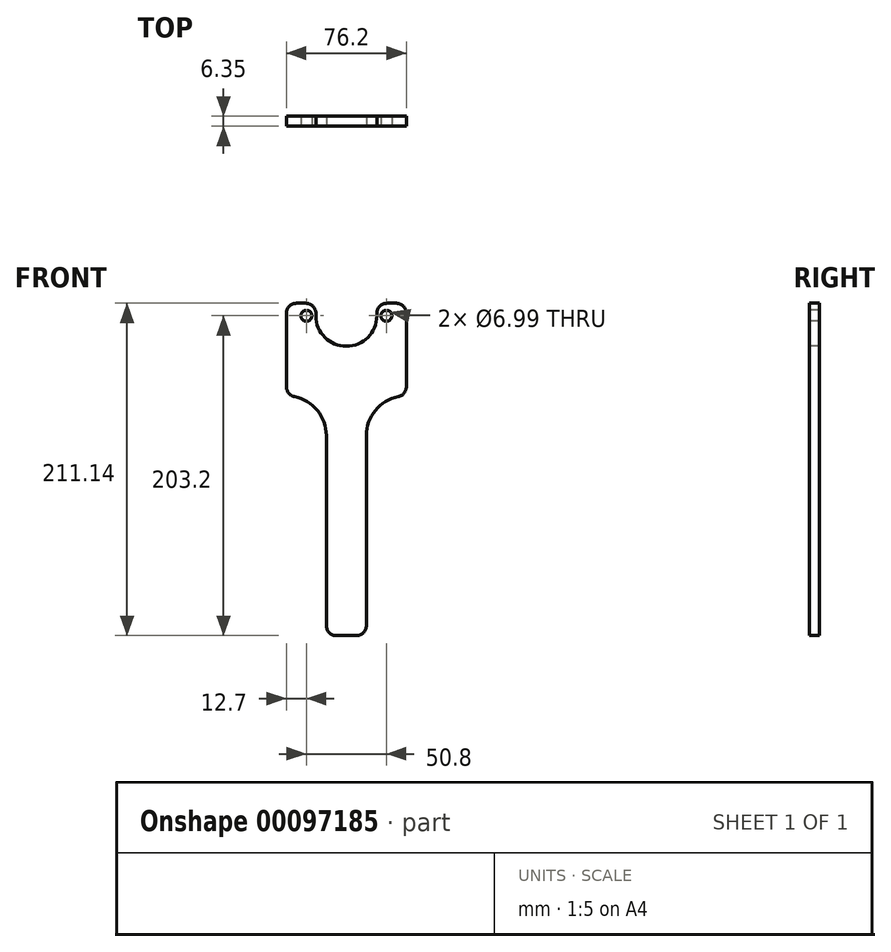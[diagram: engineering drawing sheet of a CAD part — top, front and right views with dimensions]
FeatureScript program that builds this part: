
annotation { "Feature Type Name" : "Feature", "Feature Type Description" : "" }
export const myFeature = defineFeature(function(context is Context, id is Id, definition is map)
    precondition{}
    {
        {
            var Q0;
            Q0=qCreatedBy(makeId("Front.planeOp"),FACE);
            var sketch = newSketch(context, id + "F0", { "sketchPlane" : qUnion([Q0])});
            skArc(sketch, "E0", {"start": v(-19.37, 0) * mm, "mid": v(0, -19.37) * mm, "end": v(19.37, 0) * mm});
            skLineSegment(sketch, "E1", {"start": v(-38.1, 7.94) * mm, "end": v(-38.1, -50.8) * mm});
            skLineSegment(sketch, "E2", {"start": v(-38.1, -50.8) * mm, "end": v(-38.1, -50.8) * mm});
            skLineSegment(sketch, "E3", {"start": v(-12.7, -76.2) * mm, "end": v(-12.7, -203.2) * mm});
            skLineSegment(sketch, "E4", {"start": v(-12.7, -203.2) * mm, "end": v(12.7, -203.2) * mm});
            skLineSegment(sketch, "E5", {"start": v(12.7, -203.2) * mm, "end": v(12.7, -76.2) * mm});
            skLineSegment(sketch, "E6", {"start": v(38.1, -50.8) * mm, "end": v(38.1, 7.94) * mm});
            skLineSegment(sketch, "E7", {"start": v(0, -203.2) * mm, "end": v(0, 41.77) * mm, "construction": true});
            skLineSegment(sketch, "E8", {"start": v(38.1, -50.8) * mm, "end": v(38.1, -50.8) * mm});
            skPoint(sketch, "E9.visualSharp", {"position": v(-12.7, -50.8) * mm});
            skArc(sketch, "E9.filletArc", {"start": v(-12.7, -76.2) * mm, "mid": v(-20.14, -58.24) * mm, "end": v(-38.1, -50.8) * mm});
            skPoint(sketch, "E10.visualSharp", {"position": v(12.7, -50.8) * mm});
            skArc(sketch, "E10.filletArc", {"start": v(38.1, -50.8) * mm, "mid": v(20.14, -58.24) * mm, "end": v(12.7, -76.2) * mm});
            skCircle(sketch, "E11", {"center": v(0, 0) * mm, "radius": 25.4 * mm, "construction": true});
            skCircle(sketch, "E12", {"center": v(0, 25.4) * mm, "radius": 3.5 * mm, "construction": true});
            skCircle(sketch, "E13.1.0", {"center": v(-17.96, 17.96) * mm, "radius": 3.5 * mm, "construction": true});
            skCircle(sketch, "E13.2.0", {"center": v(-25.4, 0) * mm, "radius": 3.5 * mm});
            skCircle(sketch, "E13.3.0", {"center": v(-17.96, -17.96) * mm, "radius": 3.5 * mm, "construction": true});
            skCircle(sketch, "E13.4.0", {"center": v(0, -25.4) * mm, "radius": 3.5 * mm, "construction": true});
            skCircle(sketch, "E13.5.0", {"center": v(17.96, -17.96) * mm, "radius": 3.5 * mm, "construction": true});
            skCircle(sketch, "E13.6.0", {"center": v(25.4, 0) * mm, "radius": 3.5 * mm});
            skCircle(sketch, "E13.7.0", {"center": v(17.96, 17.96) * mm, "radius": 3.5 * mm, "construction": true});
            skLineSegment(sketch, "E14", {"start": v(-38.1, 7.94) * mm, "end": v(-19.37, 7.94) * mm});
            skLineSegment(sketch, "E15", {"start": v(-19.37, 0) * mm, "end": v(-19.37, 7.94) * mm});
            skLineSegment(sketch, "E16", {"start": v(19.37, 0) * mm, "end": v(19.37, 7.94) * mm});
            skLineSegment(sketch, "E17.trimOffspring", {"start": v(19.37, 7.94) * mm, "end": v(38.1, 7.94) * mm});
            skSolve(sketch);
        }
        {
            var Q0;
            Q0 = qSketchRegion(id + "F0", true);
            extrude(context, id + "F1", {"entities" : qUnion([Q0]), "oppositeDirection" : true, "depth" : 6.35 * mm});
        }
        {
            var Q0;
            Q0=makeQuery(id+"F1.opExtrude","SWEPT_EDGE",EDGE,{"disambiguationData":[OSD([sQuery(id+"F0.wireOp",EDGE,"E1"),sQuery(id+"F0.wireOp",EDGE,"E9.filletArc")])]});
            var Q1;
            Q1=makeQuery(id+"F1.opExtrude","SWEPT_EDGE",EDGE,{"disambiguationData":[OSD([sQuery(id+"F0.wireOp",EDGE,"E6"),sQuery(id+"F0.wireOp",EDGE,"E10.filletArc")])]});
            var Q2;
            Q2=makeQuery(id+"F1.opExtrude","SWEPT_EDGE",EDGE,{"disambiguationData":[OSD([sQuery(id+"F0.wireOp",EDGE,"E6"),sQuery(id+"F0.wireOp",EDGE,"E17.trimOffspring")])]});
            var Q3;
            Q3=makeQuery(id+"F1.opExtrude","SWEPT_EDGE",EDGE,{"disambiguationData":[OSD([sQuery(id+"F0.wireOp",EDGE,"E1"),sQuery(id+"F0.wireOp",EDGE,"E14")])]});
            var Q4;
            Q4=makeQuery(id+"F1.opExtrude","SWEPT_EDGE",EDGE,{"disambiguationData":[OSD([sQuery(id+"F0.wireOp",EDGE,"E14"),sQuery(id+"F0.wireOp",EDGE,"E15")])]});
            var Q5;
            Q5=makeQuery(id+"F1.opExtrude","SWEPT_EDGE",EDGE,{"disambiguationData":[OSD([sQuery(id+"F0.wireOp",EDGE,"E16"),sQuery(id+"F0.wireOp",EDGE,"E17.trimOffspring")])]});
            var Q6;
            Q6=makeQuery(id+"F1.opExtrude","SWEPT_EDGE",EDGE,{"disambiguationData":[OSD([sQuery(id+"F0.wireOp",EDGE,"E4"),sQuery(id+"F0.wireOp",EDGE,"E5")])]});
            var Q7;
            Q7=makeQuery(id+"F1.opExtrude","SWEPT_EDGE",EDGE,{"disambiguationData":[OSD([sQuery(id+"F0.wireOp",EDGE,"E3"),sQuery(id+"F0.wireOp",EDGE,"E4")])]});
            fillet(context, id + "F2", {"entities" : qUnion([Q0, Q1, Q2, Q3, Q4, Q5, Q6, Q7]), "radius" : 6.35 * mm, "tangentPropagation" : true, "allowEdgeOverflow" : false});
        }
    });
